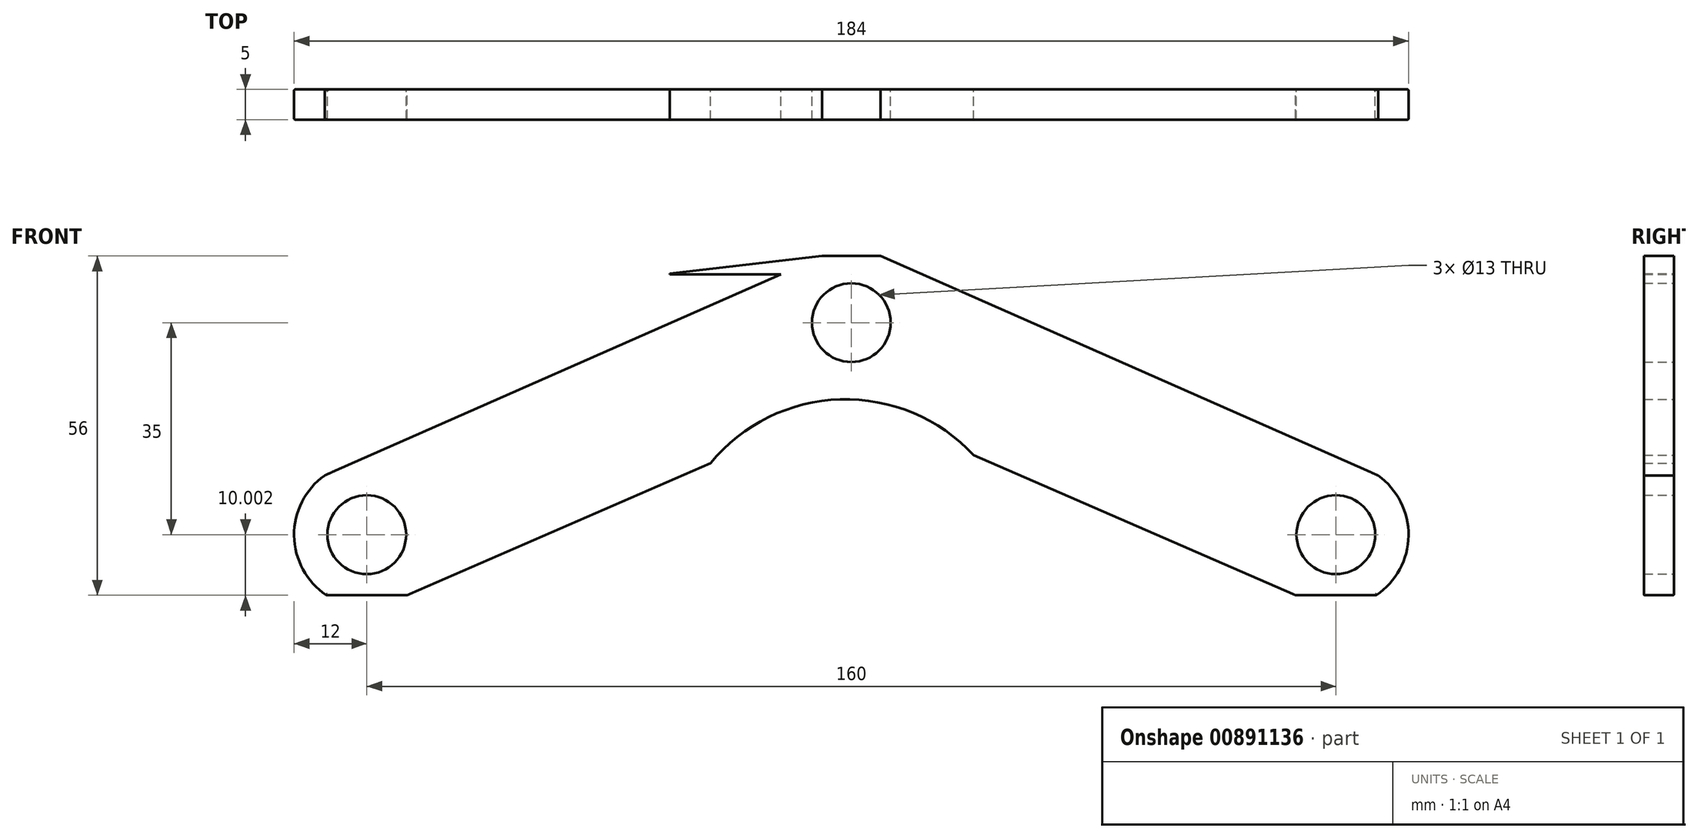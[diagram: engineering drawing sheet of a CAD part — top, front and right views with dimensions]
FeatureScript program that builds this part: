
annotation { "Feature Type Name" : "Feature", "Feature Type Description" : "" }
export const myFeature = defineFeature(function(context is Context, id is Id, definition is map)
    precondition{}
    {
        {
            var Q0;
            Q0=qCreatedBy(makeId("Front.planeOp"),FACE);
            var sketch = newSketch(context, id + "F0", { "sketchPlane" : qUnion([Q0])});
            skPoint(sketch, "E0.middle", {"position": v(0, 0) * mm});
            skLineSegment(sketch, "E1", {"start": v(0, 0) * mm, "end": v(0, 68.27) * mm, "construction": true});
            skCircle(sketch, "E2", {"center": v(-80, -11.8) * mm, "radius": 6.5 * mm});
            skCircle(sketch, "E3.MirrorC", {"center": v(80, -11.8) * mm, "radius": 6.5 * mm});
            skCircle(sketch, "E4", {"center": v(0, 23.2) * mm, "radius": 6.5 * mm});
            skArc(sketch, "E5", {"start": v(-86.96, -2.03) * mm, "mid": v(-92, -12) * mm, "end": v(-86.63, -21.8) * mm});
            skArc(sketch, "E6.MirrorC", {"start": v(86.96, -2.03) * mm, "mid": v(92, -12) * mm, "end": v(86.63, -21.8) * mm});
            skPoint(sketch, "E7.startSnap0", {"position": v(-89.77, -18.76) * mm});
            skLineSegment(sketch, "E8", {"start": v(-86.63, -21.8) * mm, "end": v(-73.37, -21.8) * mm});
            skLineSegment(sketch, "E9.trimOffspring", {"start": v(-73.37, -21.8) * mm, "end": v(-73.37, -21.8) * mm});
            skLineSegment(sketch, "E10.trimOffspring", {"start": v(73.37, -21.8) * mm, "end": v(86.63, -21.8) * mm});
            skArc(sketch, "E11.trimOffspring", {"start": v(73.37, -21.8) * mm, "mid": v(73.2, -21.69) * mm, "end": v(73.04, -21.57) * mm});
            skLineSegment(sketch, "E12", {"start": v(-86.96, -2.03) * mm, "end": v(-11.64, 31.2) * mm});
            skLineSegment(sketch, "E13", {"start": v(86.96, -2.03) * mm, "end": v(4.84, 34.2) * mm});
            skLineSegment(sketch, "E14", {"start": v(-73.37, -21.8) * mm, "end": v(-23.25, 0) * mm});
            skLineSegment(sketch, "E15", {"start": v(20.22, 1.32) * mm, "end": v(73.37, -21.8) * mm});
            skLineSegment(sketch, "E16", {"start": v(-4.84, 34.2) * mm, "end": v(4.84, 34.2) * mm});
            skLineSegment(sketch, "E17.top", {"start": v(-11.64, 31.2) * mm, "end": v(-30, 31.2) * mm});
            skArc(sketch, "E18", {"start": v(20.22, 1.32) * mm, "mid": v(-1.82, 10.53) * mm, "end": v(-23.25, 0) * mm});
            skLineSegment(sketch, "E19", {"start": v(-30, 31.2) * mm, "end": v(-30, 31.3) * mm});
            skPoint(sketch, "E20.start.orphan", {"position": v(-21.27, 34.18) * mm});
            skPoint(sketch, "E21.end.orphan", {"position": v(-20, 34.18) * mm});
            skLineSegment(sketch, "E22", {"start": v(-30, 31.3) * mm, "end": v(-4.84, 34.2) * mm});
            skSolve(sketch);
        }
        {
            var Q0;
            Q0 = qSketchRegion(id + "F0", true);
            extrude(context, id + "F1", {"entities" : qUnion([Q0]), "depth" : 5 * mm, "offsetDistance" : 25 * mm});
        }
        {
            var Q0;
            Q0=makeQuery(id+"F1.opExtrude","CAP_EDGE",EDGE,{"disambiguationData":[OSD([sQuery(id+"F0.wireOp",EDGE,"6Diu7GIx-gYES-30c8-VpNu-9I4aw0HdvodG")])],"isStart":false});
            var Q1;
            Q1=makeQuery(id+"F1.opExtrude","CAP_EDGE",EDGE,{"disambiguationData":[OSD([sQuery(id+"F0.wireOp",EDGE,"FzQQHwxz-MGj0-pd6q-Vwkf-SxTCfIyFQYqu")])],"isStart":false});
            var Q2;
            Q2=makeQuery(id+"F1.opExtrude","CAP_EDGE",EDGE,{"disambiguationData":[OSD([sQuery(id+"F0.wireOp",EDGE,"E5")])],"isStart":false});
            var Q3;
            Q3=makeQuery(id+"F1.opExtrude","CAP_EDGE",EDGE,{"disambiguationData":[OSD([sQuery(id+"F0.wireOp",EDGE,"TmPSW8hT-ZDWS-5P5V-NTUT-m0BjZDoPljxY")])],"isStart":false});
            var Q4;
            Q4=makeQuery(id+"F1.opExtrude","CAP_EDGE",EDGE,{"disambiguationData":[OSD([sQuery(id+"F0.wireOp",EDGE,"tW4D9efH-LhZ5-ztnQ-unpH-8nhIlHPKTfGy")])],"isStart":false});
            var Q5;
            Q5=makeQuery(id+"F1.opExtrude","CAP_EDGE",EDGE,{"disambiguationData":[OSD([sQuery(id+"F0.wireOp",EDGE,"tW4D9efH-LhZ5-ztnQ-unpH-8nhIlHPKTfGy")])],"isStart":true});
            var Q6;
            Q6=makeQuery(id+"F1.opExtrude","CAP_EDGE",EDGE,{"disambiguationData":[OSD([sQuery(id+"F0.wireOp",EDGE,"975bcda2-a192-4684-8842-a333f1ca748d0.MirrorCS")])],"isStart":true});
            var Q7;
            Q7=makeQuery(id+"F1.opExtrude","CAP_EDGE",EDGE,{"disambiguationData":[OSD([sQuery(id+"F0.wireOp",EDGE,"975bcda2-a192-4684-8842-a333f1ca748d0.MirrorCS")])],"isStart":false});
            var Q8;
            Q8=makeQuery(id+"F1.opExtrude","CAP_EDGE",EDGE,{"disambiguationData":[OSD([sQuery(id+"F0.wireOp",EDGE,"TmPSW8hT-ZDWS-5P5V-NTUT-m0BjZDoPljxY")])],"isStart":true});
            var Q9;
            Q9=makeQuery(id+"F1.opExtrude","CAP_EDGE",EDGE,{"disambiguationData":[OSD([sQuery(id+"F0.wireOp",EDGE,"E6.MirrorC")])],"isStart":true});
            var Q10;
            Q10=makeQuery(id+"F1.opExtrude","CAP_EDGE",EDGE,{"disambiguationData":[OSD([sQuery(id+"F0.wireOp",EDGE,"E6.MirrorC")])],"isStart":false});
            var Q11;
            Q11=makeQuery(id+"F1.opExtrude","CAP_EDGE",EDGE,{"disambiguationData":[OSD([sQuery(id+"F0.wireOp",EDGE,"FzQQHwxz-MGj0-pd6q-Vwkf-SxTCfIyFQYqu")])],"isStart":true});
            var Q12;
            Q12=makeQuery(id+"F1.opExtrude","CAP_EDGE",EDGE,{"disambiguationData":[OSD([sQuery(id+"F0.wireOp",EDGE,"E5")])],"isStart":true});
            var Q13;
            Q13=makeQuery(id+"F1.opExtrude","CAP_EDGE",EDGE,{"disambiguationData":[OSD([sQuery(id+"F0.wireOp",EDGE,"6Diu7GIx-gYES-30c8-VpNu-9I4aw0HdvodG")])],"isStart":true});
            var Q14;
            Q14=makeQuery(id+"F1.opExtrude","CAP_EDGE",EDGE,{"disambiguationData":[OSD([sQuery(id+"F0.wireOp",EDGE,"c9ZcgPeJ-fKaD-NiF3-xaad-thTHOOLCtYlH")])],"isStart":true});
            var Q15;
            Q15=makeQuery(id+"F1.opExtrude","CAP_EDGE",EDGE,{"disambiguationData":[OSD([sQuery(id+"F0.wireOp",EDGE,"PRH0V9Sd-zkaX-8TMp-sbTS-UZTvKAs4ANJF.top")])],"isStart":true});
            var Q16;
            Q16=makeQuery(id+"F1.opExtrude","SWEPT_EDGE",EDGE,{"disambiguationData":[OSD([sQuery(id+"F0.wireOp",EDGE,"975bcda2-a192-4684-8842-a333f1ca748d0.MirrorCS"),sQuery(id+"F0.wireOp",EDGE,"cTzfg4Vt-Rzme-nW9z-NYM4-IZY6k5av88b8")])]});
            var Q17;
            Q17=makeQuery(id+"F1.opExtrude","CAP_EDGE",EDGE,{"disambiguationData":[OSD([sQuery(id+"F0.wireOp",EDGE,"PRH0V9Sd-zkaX-8TMp-sbTS-UZTvKAs4ANJF.right")])],"isStart":true});
            var Q18;
            Q18=makeQuery(id+"F1.opExtrude","SWEPT_EDGE",EDGE,{"disambiguationData":[OSD([sQuery(id+"F0.wireOp",EDGE,"PRH0V9Sd-zkaX-8TMp-sbTS-UZTvKAs4ANJF.top"),sQuery(id+"F0.wireOp",EDGE,"PRH0V9Sd-zkaX-8TMp-sbTS-UZTvKAs4ANJF.right")])]});
            var Q19;
            Q19=makeQuery(id+"F1.opExtrude","CAP_EDGE",EDGE,{"disambiguationData":[OSD([sQuery(id+"F0.wireOp",EDGE,"PRH0V9Sd-zkaX-8TMp-sbTS-UZTvKAs4ANJF.right")])],"isStart":false});
            var Q20;
            Q20=makeQuery(id+"F1.opExtrude","SWEPT_EDGE",EDGE,{"disambiguationData":[OSD([sQuery(id+"F0.wireOp",EDGE,"PRH0V9Sd-zkaX-8TMp-sbTS-UZTvKAs4ANJF.bottom"),sQuery(id+"F0.wireOp",EDGE,"PRH0V9Sd-zkaX-8TMp-sbTS-UZTvKAs4ANJF.right")])]});
            var Q21;
            Q21=makeQuery(id+"F1.opExtrude","CAP_EDGE",EDGE,{"disambiguationData":[OSD([sQuery(id+"F0.wireOp",EDGE,"c9ZcgPeJ-fKaD-NiF3-xaad-thTHOOLCtYlH")])],"isStart":false});
            var Q22;
            Q22=makeQuery(id+"F1.opExtrude","CAP_EDGE",EDGE,{"disambiguationData":[OSD([sQuery(id+"F0.wireOp",EDGE,"PRH0V9Sd-zkaX-8TMp-sbTS-UZTvKAs4ANJF.top")])],"isStart":false});
            fillet(context, id + "F2", {"entities" : qUnion([Q0, Q1, Q2, Q3, Q4, Q5, Q6, Q7, Q8, Q9, Q10, Q11, Q12, Q13, Q14, Q15, Q16, Q17, Q18, Q19, Q20, Q21, Q22]), "radius" : 0.2 * mm, "tangentPropagation" : true, "allowEdgeOverflow" : false});
        }
        {
            var Q0;
            Q0=makeQuery(id+"F1.opExtrude","CAP_EDGE",EDGE,{"disambiguationData":[OSD([sQuery(id+"F0.wireOp",EDGE,"E10.trimOffspring")])],"isStart":false});
            var Q1;
            Q1=makeQuery(id+"F1.opExtrude","CAP_EDGE",EDGE,{"disambiguationData":[OSD([sQuery(id+"F0.wireOp",EDGE,"E10.trimOffspring")])],"isStart":true});
            var Q2;
            Q2=makeQuery(id+"F1.opExtrude","CAP_EDGE",EDGE,{"disambiguationData":[OSD([sQuery(id+"F0.wireOp",EDGE,"E8")])],"isStart":false});
            var Q3;
            Q3=makeQuery(id+"F1.opExtrude","CAP_EDGE",EDGE,{"disambiguationData":[OSD([sQuery(id+"F0.wireOp",EDGE,"E8")])],"isStart":true});
            fillet(context, id + "F3", {"entities" : qUnion([Q0, Q1, Q2, Q3]), "radius" : 0.2 * mm, "tangentPropagation" : true, "allowEdgeOverflow" : false});
        }
    });
